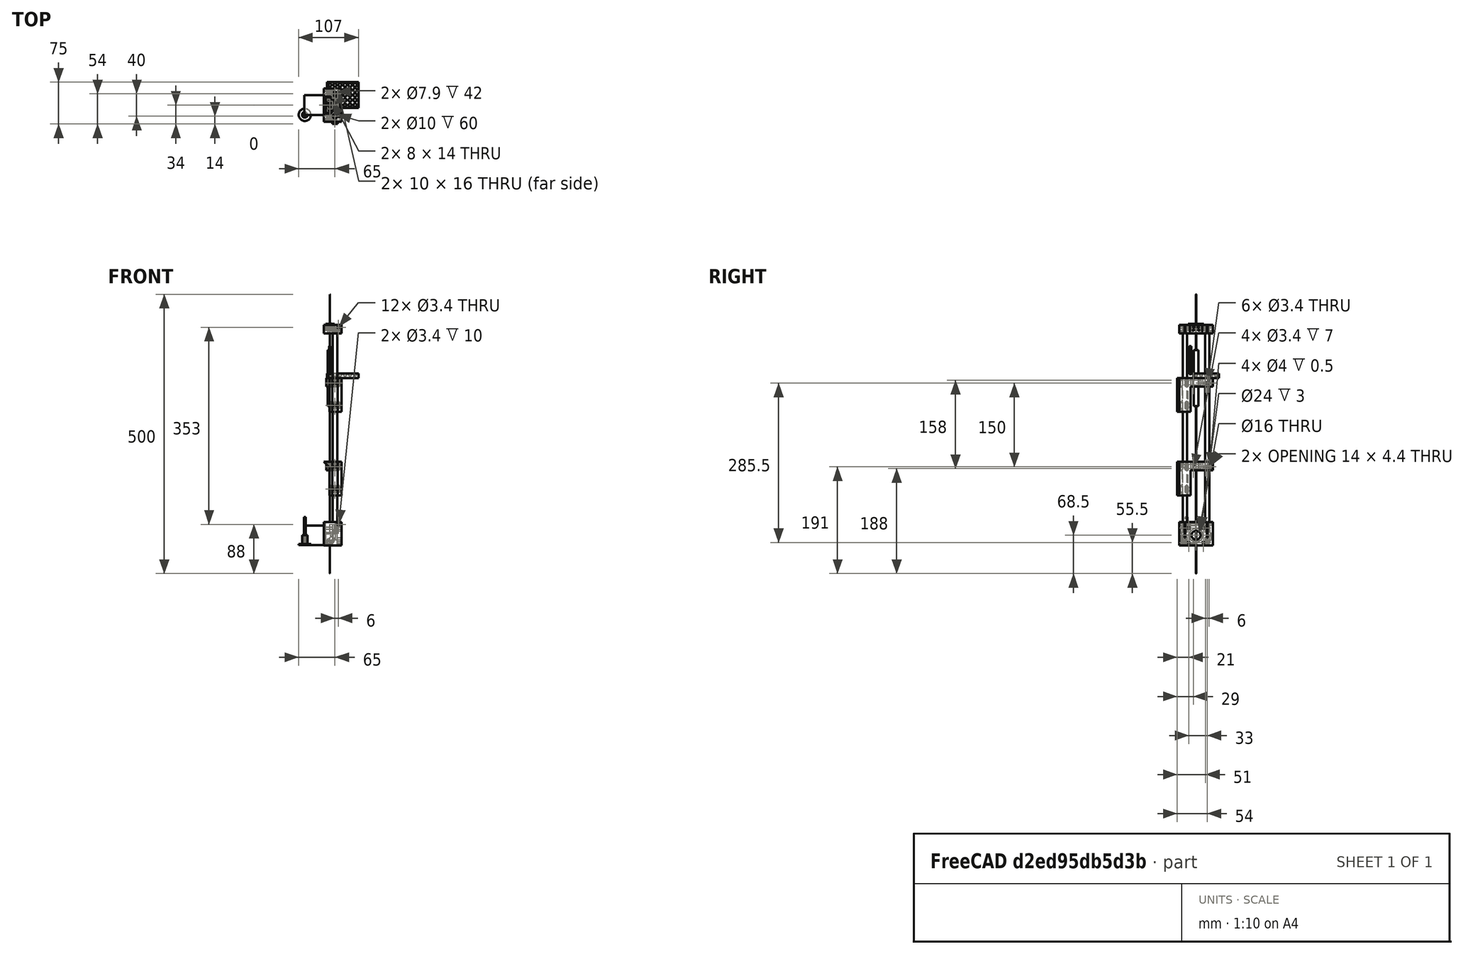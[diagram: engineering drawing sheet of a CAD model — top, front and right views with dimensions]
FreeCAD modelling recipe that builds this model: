
FCSTD DOCUMENT  (FreeCAD 0.16R6703 (Git))
Label: lorenz
License: All rights reserved
LicenseURL: http://en.wikipedia.org/wiki/All_rights_reserved
objects: Part::Cut×73, Part::Feature×49, Part::Cylinder×34, Part::Box×32, Part::Fuse×28, Part::Chamfer×13, Part::Sphere×7, Part::Sweep×6, App::DocumentObjectGroup×5, Part::Mirroring×5, Part::Circle×3, Part::Cone×2, Part::MultiCommon×1
note: 253 computed .brp shape members not serialized (recipe doc carries the construction recipe); baked Part::Feature solids carry a one-line shape summary decoded from their .brp

FEATURE [Part::Sphere] Sphere
  Angle1 = -90
  Angle2 = 90
  Angle3 = 360
  Placement = pos=(0,0,6) rot=(0,0,1;0rad)
  Radius = 3
FEATURE [Part::Box] Box112015002017004007003  label="Cube089"
  Height = 8
  Length = 56
  Placement = pos=(-5,-5,0) rot=(0,0,1;0rad)
  Width = 46
FEATURE [Part::Feature] Sphere001 .. Sphere005  x5 (patterned run collapsed; names and placements below)
  shape: bbox 6 x 6 x 6 mm, 1 faces (baked)
  placements: 5 in arithmetic series — first pos=(9,0,6.3) rot=(0,0,1;0rad), step (9,0,0.3), last pos=(45,0,7.5) rot=(0,0,1;0rad)
FEATURE [Part::Sphere] Sphere006
  Angle1 = -90
  Angle2 = 90
  Angle3 = 360
  Placement = pos=(0,9,6) rot=(0,0,1;0rad)
  Radius = 3.1
FEATURE [Part::Feature] Sphere006001 .. Sphere006005  x5 (patterned run collapsed; names and placements below)
  shape: bbox 6.2 x 6.2 x 6.2 mm, 1 faces (baked)
  placements: 5 in arithmetic series — first pos=(9,9,6.3) rot=(0,0,1;0rad), step (9,0,0.3), last pos=(45,9,7.5) rot=(0,0,1;0rad)
FEATURE [Part::Sphere] Sphere006006
  Angle1 = -90
  Angle2 = 90
  Angle3 = 360
  Placement = pos=(0,18,6) rot=(0,0,1;0rad)
  Radius = 3.2
FEATURE [Part::Feature] Sphere006006001 .. Sphere006006005  x5 (patterned run collapsed; names and placements below)
  shape: bbox 6.4 x 6.4 x 6.4 mm, 1 faces (baked)
  placements: 5 in arithmetic series — first pos=(9,18,6.3) rot=(0,0,1;0rad), step (9,0,0.3), last pos=(45,18,7.5) rot=(0,0,1;0rad)
FEATURE [Part::Sphere] Sphere006006006
  Angle1 = -90
  Angle2 = 90
  Angle3 = 360
  Placement = pos=(0,27,6) rot=(0,0,1;0rad)
  Radius = 3.3
FEATURE [Part::Feature] Sphere006006006001 .. Sphere006006006005  x5 (patterned run collapsed; names and placements below)
  shape: bbox 6.6 x 6.6 x 6.6 mm, 1 faces (baked)
  placements: 5 in arithmetic series — first pos=(9,27,6.3) rot=(0,0,1;0rad), step (9,0,0.3), last pos=(45,27,7.5) rot=(0,0,1;0rad)
FEATURE [Part::Sphere] Sphere006006006006
  Angle1 = -90
  Angle2 = 90
  Angle3 = 360
  Placement = pos=(0,36,6) rot=(0,0,1;0rad)
  Radius = 3.4
FEATURE [Part::Feature] Sphere006006006006001 .. Sphere006006006006005  x5 (patterned run collapsed; names and placements below)
  shape: bbox 6.8 x 6.8 x 6.8 mm, 1 faces (baked)
  placements: 5 in arithmetic series — first pos=(9,36,6.3) rot=(0,0,1;0rad), step (9,0,0.3), last pos=(45,36,7.5) rot=(0,0,1;0rad)
FEATURE [Part::Cut] Cut175
  Base = -> Box112015002017004007003
  Tool = -> Sphere
FEATURE [Part::Cut] Cut176
  Base = -> Cut175
  Tool = -> Sphere006006006006005
FEATURE [Part::Cut] Cut177
  Base = -> Cut176
  Tool = -> Sphere006006006006004
FEATURE [Part::Cut] Cut178
  Base = -> Cut177
  Tool = -> Sphere006006006006003
FEATURE [Part::Cut] Cut179
  Base = -> Cut178
  Tool = -> Sphere006006006006002
FEATURE [Part::Cut] Cut180
  Base = -> Cut179
  Tool = -> Sphere006006006006001
FEATURE [Part::Cut] Cut181
  Base = -> Cut180
  Tool = -> Sphere006006006006
FEATURE [Part::Cut] Cut182
  Base = -> Cut181
  Tool = -> Sphere006006006005
FEATURE [Part::Cut] Cut183
  Base = -> Cut182
  Tool = -> Sphere006006006004
FEATURE [Part::Cut] Cut184
  Base = -> Cut183
  Tool = -> Sphere006006006003
FEATURE [Part::Cut] Cut185
  Base = -> Cut184
  Tool = -> Sphere006006006002
FEATURE [Part::Cut] Cut186
  Base = -> Cut185
  Tool = -> Sphere006006006001
FEATURE [Part::Cut] Cut187
  Base = -> Cut186
  Tool = -> Sphere006006006
FEATURE [Part::Cut] Cut188
  Base = -> Cut187
  Tool = -> Sphere006006005
FEATURE [Part::Cut] Cut189
  Base = -> Cut188
  Tool = -> Sphere006006004
FEATURE [Part::Cut] Cut190
  Base = -> Cut189
  Tool = -> Sphere006006003
FEATURE [Part::Cut] Cut191
  Base = -> Cut190
  Tool = -> Sphere006006002
FEATURE [Part::Cut] Cut192
  Base = -> Cut191
  Tool = -> Sphere006006001
FEATURE [Part::Cut] Cut193
  Base = -> Cut192
  Tool = -> Sphere006006
FEATURE [Part::Cut] Cut194
  Base = -> Cut193
  Tool = -> Sphere006005
FEATURE [Part::Cut] Cut195
  Base = -> Cut194
  Tool = -> Sphere006004
FEATURE [Part::Cut] Cut196
  Base = -> Cut195
  Tool = -> Sphere006003
FEATURE [Part::Cut] Cut197
  Base = -> Cut196
  Tool = -> Sphere006002
FEATURE [Part::Cut] Cut198
  Base = -> Cut197
  Tool = -> Sphere006001
FEATURE [Part::Cut] Cut199
  Base = -> Cut198
  Tool = -> Sphere006
FEATURE [Part::Cut] Cut200
  Base = -> Cut199
  Tool = -> Sphere005
FEATURE [Part::Cut] Cut201
  Base = -> Cut200
  Tool = -> Sphere004
FEATURE [Part::Cut] Cut202
  Base = -> Cut201
  Tool = -> Sphere003
FEATURE [Part::Cut] Cut203
  Base = -> Cut202
  Tool = -> Sphere002
FEATURE [Part::Cut] Cut204
  Base = -> Cut203
  Tool = -> Sphere001
FEATURE [Part::Chamfer] Chamfer006012003  label="ball-socket-test"
  Base = -> Cut204
  Edges = 1 edges r=2: [Edge1]
FEATURE [App::DocumentObjectGroup] Group002  label="Experiments"
  Group = -> [Chamfer006012003]
FEATURE [Part::Box] Box112015002017004007004016  label="Cube099"
  Height = 14
  Length = 4.4
  Placement = pos=(-2.2,-2,-4) rot=(0,0,1;0rad)
  Width = 4
FEATURE [Part::Chamfer] Chamfer006012018
  Base = -> Box112015002017004007004016
  Edges = 1 edges r=2: [Edge6]
FEATURE [Part::Chamfer] Chamfer006012019
  Base = -> Chamfer006012018
  Edges = 1 edges r=2: [Edge15]
  Placement = pos=(0,0,2) rot=(0,0,1;0rad)
FEATURE [Part::Chamfer] Chamfer003
  Base = -> Chamfer006012019
  Edges = 1 edges r=2: [Edge14]
FEATURE [Part::Chamfer] Chamfer006012020  label="PTFE-slot-002"
  Base = -> Chamfer003
  Edges = 1 edges r=2: [Edge16]
  Placement = pos=(0,-6.25,0) rot=(0,0,1;0rad)
FEATURE [Part::Feature] Fusion051010010012015014001  label="reactor-slot-1"
  Placement = pos=(5.41266,3.125,0) rot=(0,0,1;2.0944rad)
  shape: bbox 5.997 x 5.887 x 14 mm, 14 faces (baked)
FEATURE [Part::Feature] Fusion051010010012015014002  label="reactor-slot-2"
  Placement = pos=(-5.41266,3.125,0) rot=(0,0,1;4.18879rad)
  shape: bbox 5.997 x 5.887 x 14 mm, 14 faces (baked)
FEATURE [Part::Cylinder] Cylinder054029  label="M4-adjuster"
  Angle = 360
  Height = 20
  Placement = pos=(0,-5,5) rot=(1,0,0;1.5708rad)
  Radius = 1.7
FEATURE [Part::Fuse] Fusion051010010012015014003  label="adjuster-slot"
  Base = -> Chamfer006012020
  Tool = -> Cylinder054029
FEATURE [Part::Cylinder] Cylinder054031  label="steel002"
  Angle = 360
  Height = 200
  Placement = pos=(0,0,-100) rot=(0,0,1;0rad)
  Radius = 5
FEATURE [Part::Box] Box112015002017004007004017  label="Cube100"
  Height = 16
  Length = 16
  Placement = pos=(0,-30,0) rot=(0,0,1;0rad)
  Width = 60
FEATURE [Part::Box] Box112015002017004007004018  label="Cube101"
  Height = 20
  Length = 100
  Placement = pos=(-50,-50,-28) rot=(0,0,1;0rad)
  Width = 100
FEATURE [Part::Sphere] Sphere006006006006008
  Angle1 = -90
  Angle2 = 90
  Angle3 = 360
  Placement = pos=(8,25,1.2) rot=(0,0,1;0rad)
  Radius = 3.05
FEATURE [Part::Sphere] Sphere006006006006009
  Angle1 = -90
  Angle2 = 90
  Angle3 = 360
  Placement = pos=(8,-25,1.2) rot=(0,0,1;0rad)
  Radius = 3.05
FEATURE [Part::Cut] Cut253
  Base = -> Box112015002017004007004017
  Tool = -> Sphere006006006006008
FEATURE [Part::Cut] Cut254
  Base = -> Cut253
  Placement = pos=(-22,0,3) rot=(0,1,0;2.35619rad)
  Tool = -> Sphere006006006006009
FEATURE [Part::Cut] Cut255  label="socket-bar001"
  Base = -> Cut254
  Placement = pos=(22,0,-8) rot=(1,0,0;3.14159rad)
  Tool = -> Box112015002017004007004018
FEATURE [Part::Fuse] Fusion051010010012015014004
  Base = -> Fusion051010010012015014001
  Tool = -> Fusion051010010012015014002
FEATURE [Part::Fuse] Fusion051010010012015014005
  Base = -> Fusion051010010012015014003
  Tool = -> Fusion051010010012015014004
FEATURE [Part::Fuse] Fusion051010010012015014006  label="bearing-cavity-3a"
  Base = -> Cylinder054031
  Placement = pos=(9,-20,-4) rot=(0,1,0;3.14159rad)
  Tool = -> Fusion051010010012015014005
FEATURE [Part::Box] Box112015002017004007004019  label="Cube102"
  Height = 14
  Length = 4.4
  Placement = pos=(-2.2,-2,-4) rot=(0,0,1;0rad)
  Width = 4
FEATURE [Part::Chamfer] Chamfer006012021
  Base = -> Box112015002017004007004019
  Edges = 1 edges r=2: [Edge6]
FEATURE [Part::Chamfer] Chamfer006012022
  Base = -> Chamfer006012021
  Edges = 1 edges r=2: [Edge15]
  Placement = pos=(0,0,2) rot=(0,0,1;0rad)
FEATURE [Part::Chamfer] Chamfer006012023
  Base = -> Chamfer006012022
  Edges = 1 edges r=2: [Edge14]
FEATURE [Part::Chamfer] Chamfer006012024  label="PTFE-slot-003"
  Base = -> Chamfer006012023
  Edges = 1 edges r=2: [Edge16]
  Placement = pos=(0,-6.25,0) rot=(0,0,1;0rad)
FEATURE [Part::Cylinder] Cylinder054032  label="M4-adjuster001"
  Angle = 360
  Height = 20
  Placement = pos=(0,-5,5) rot=(1,0,0;1.5708rad)
  Radius = 1.7
FEATURE [Part::Fuse] Fusion051010010012015014007  label="adjuster-slot001"
  Base = -> Chamfer006012024
  Placement = pos=(-5,0,0) rot=(0,1,0;1.5708rad)
  Tool = -> Cylinder054032
FEATURE [Part::Feature] Fusion051010010012015014008  label="reactor-slot-003"
  Placement = pos=(-5,6.25,-6.13174e-07) rot=(0.707107,0,0.707107;3.14159rad)
  shape: bbox 14 x 4.5 x 4.4 mm, 14 faces (baked)
FEATURE [Part::Box] Box112015002017004007004020  label="Cube103"
  Height = 200
  Length = 16
  Placement = pos=(-8,-5,-100) rot=(0,0,1;0rad)
  Width = 10
FEATURE [Part::Fuse] Fusion051010010012015014009
  Base = -> Fusion051010010012015014008
  Tool = -> Box112015002017004007004020
FEATURE [Part::Fuse] Fusion051010010012015014010  label="bearing-cavity-2a"
  Base = -> Fusion051010010012015014007
  Placement = pos=(9,20,-9) rot=(-0.707107,0.707107,0;3.14159rad)
  Tool = -> Fusion051010010012015014009
FEATURE [Part::Fuse] Fusion051010010012015014013  label="bearing-cavity-3a001"
  Base = -> Cylinder054031
  Placement = pos=(9,-20,-44) rot=(0,1,0;3.14159rad)
  Tool = -> Fusion051010010012015014005
FEATURE [Part::Box] Box112015002017004007004021  label="Cube104"
  Height = 60
  Length = 22
  Placement = pos=(-1,-30,0) rot=(0,0,1;0rad)
  Width = 60
FEATURE [Part::Box] Box112015002017004007004022  label="Cube105"
  Height = 60
  Length = 24
  Placement = pos=(-2,-50,15) rot=(0,0,1;0rad)
  Width = 60
FEATURE [Part::Box] Box112015002017004007004023  label="Cube106"
  Height = 60
  Length = 10
  Placement = pos=(4,24,0) rot=(0,0,1;0rad)
  Width = 10
FEATURE [Part::Fuse] Fusion051010010012015014014
  Base = -> Box112015002017004007004021
  Tool = -> Box112015002017004007004023
FEATURE [Part::Cut] Cut256
  Base = -> Fusion051010010012015014014
  Placement = pos=(0,0,0) rot=(1,0,0;3.14159rad)
  Tool = -> Box112015002017004007004022
FEATURE [Part::Cylinder] Cylinder054033  label="centreline"
  Angle = 360
  Height = 500
  Placement = pos=(0,0,-350) rot=(0,0,1;0rad)
  Radius = 0.1
FEATURE [Part::Box] Box112015002017004007004024  label="wire-clamp-slot001"
  Height = 30
  Length = 1
  Placement = pos=(-0.5,-6,-19) rot=(0,0,1;0rad)
  Width = 2
FEATURE [Part::Cylinder] Cylinder054035  label="wire-clamp-screw-hole-1"
  Angle = 360
  Height = 10
  Placement = pos=(-9.5,-5,-4) rot=(0,1,0;1.5708rad)
  Radius = 1.7
FEATURE [Part::Cylinder] Cylinder054036  label="wire-clamp-screw-hole-2"
  Angle = 360
  Height = 10
  Placement = pos=(-9.5,-5,-12) rot=(0,1,0;1.5708rad)
  Radius = 1.7
FEATURE [Part::Box] Box112015002017004007004025  label="Cube108"
  Height = 15
  Length = 6
  Placement = pos=(-6.5,-9,-15) rot=(0,0,1;0rad)
  Width = 18
FEATURE [Part::Box] Box112015002017004007004026  label="wire-slot"
  Height = 30
  Length = 8
  Placement = pos=(-4,4,-19) rot=(0,0,1;0rad)
  Width = 2
FEATURE [Part::Cylinder] Cylinder054037  label="steel-3"
  Angle = 360
  Height = 395
  Placement = pos=(9,-20,-300) rot=(0,0,1;0rad)
  Radius = 4
FEATURE [Part::Cylinder] Cylinder054038  label="steel-2"
  Angle = 360
  Height = 395
  Placement = pos=(9,20,-300) rot=(0,0,1;0rad)
  Radius = 4
FEATURE [Part::Box] Box112015002017004007004027  label="Cube110"
  Height = 42
  Length = 32
  Placement = pos=(-11,-30,-1) rot=(0,0,1;0rad)
  Width = 60
FEATURE [Part::Box] Box112015002017004007004028  label="Cube111"
  Height = 35
  Length = 35
  Placement = pos=(-46,-17.5,-299) rot=(0,0,1;0rad)
  Width = 35
FEATURE [Part::Cylinder] Cylinder054039  label="drive"
  Angle = 360
  Height = 18
  Placement = pos=(-45,-17.5,-299) rot=(0,0,1;0rad)
  Radius = 5
FEATURE [Part::Cylinder] Cylinder054040  label="boss"
  Angle = 360
  Height = 2
  Placement = pos=(-45,-17.5,-299) rot=(0,0,1;0rad)
  Radius = 11
FEATURE [Part::Cylinder] Cylinder054041  label="M3-1"
  Angle = 360
  Height = 50
  Placement = pos=(-45,-17.5,-299) rot=(0,0,1;0rad)
  Radius = 1.7
FEATURE [Part::Cylinder] Cylinder054042  label="M3-2"
  Angle = 360
  Height = 50
  Placement = pos=(-45,-17.5,-299) rot=(0,0,1;0rad)
  Radius = 1.7
FEATURE [Part::Cylinder] Cylinder054043  label="M3-3"
  Angle = 360
  Height = 50
  Placement = pos=(-45,-17.5,-299) rot=(0,0,1;0rad)
  Radius = 1.7
FEATURE [Part::Cylinder] Cylinder054044  label="M3-4"
  Angle = 360
  Height = 50
  Placement = pos=(-45,-17.5,-299) rot=(0,0,1;0rad)
  Radius = 1.7
FEATURE [App::DocumentObjectGroup] Group005  label="NEMA-14"
  Group = -> [Box112015002017004007004028,Cylinder054039,Cylinder054040,Cylinder054041,Cylinder054042,Cylinder054043,Cylinder054044]
FEATURE [Part::Cylinder] Cylinder054045  label="boss001"
  Angle = 360
  Height = 3
  Placement = pos=(-11,0,17.5) rot=(0,1,0;1.5708rad)
  Radius = 12
FEATURE [Part::Cut] Cut264
  Base = -> Box112015002017004007004027
  Tool = -> Cylinder054045
FEATURE [Part::Cylinder] Cylinder054046  label="M3-005"
  Angle = 360
  Height = 50
  Placement = pos=(-12,13,30.5) rot=(0,1,0;1.5708rad)
  Radius = 1.7
FEATURE [Part::Cylinder] Cylinder054047  label="M3-006"
  Angle = 360
  Height = 50
  Placement = pos=(-12,-13,4.5) rot=(0,1,0;1.5708rad)
  Radius = 1.7
FEATURE [Part::Cylinder] Cylinder054048  label="M3-007"
  Angle = 360
  Height = 50
  Placement = pos=(-12,13,4.5) rot=(0,1,0;1.5708rad)
  Radius = 1.7
FEATURE [Part::Cylinder] Cylinder054049  label="M3-008"
  Angle = 360
  Height = 50
  Placement = pos=(-12,-13,30.5) rot=(0,1,0;1.5708rad)
  Radius = 1.7
FEATURE [Part::Cut] Cut265
  Base = -> Cut264
  Tool = -> Cylinder054046
FEATURE [Part::Cut] Cut266
  Base = -> Cut265
  Tool = -> Cylinder054049
FEATURE [Part::Cut] Cut267
  Base = -> Cut266
  Tool = -> Cylinder054048
FEATURE [Part::Cut] Cut268
  Base = -> Cut267
  Tool = -> Cylinder054047
FEATURE [Part::Cylinder] Cylinder054050  label="drive001"
  Angle = 360
  Height = 40
  Placement = pos=(-9,0,17.5) rot=(0,1,0;1.5708rad)
  Radius = 8
FEATURE [Part::Cut] Cut269
  Base = -> Cut268
  Tool = -> Cylinder054050
FEATURE [Part::Box] Box112015002017004007004029  label="Cube112"
  Height = 50
  Length = 18
  Placement = pos=(-8,-10,9) rot=(0,0,1;0rad)
  Width = 20
FEATURE [Part::Cut] Cut270
  Base = -> Cut269
  Tool = -> Box112015002017004007004029
FEATURE [Part::Cylinder] Cylinder054051  label="grub-003"
  Angle = 360
  Height = 30
  Placement = pos=(-28,26,32) rot=(1,0,0;1.5708rad)
  Radius = 1.7
FEATURE [Part::Box] Box112015002017004007004030  label="Cube113"
  Height = 33
  Length = 5.3
  Placement = pos=(-30.65,6,29) rot=(0,0,1;0rad)
  Width = 2.5
FEATURE [Part::Fuse] Fusion051010010012015014017  label="nut-trap"
  Base = -> Cylinder054051
  Placement = pos=(43,5,5) rot=(0,0,1;0rad)
  Tool = -> Box112015002017004007004030
FEATURE [Part::Box] Box112015002017004007004031  label="Cube114"
  Height = 50
  Length = 15
  Placement = pos=(10,19.25,13) rot=(0,0,1;0rad)
  Width = 1.5
FEATURE [Part::Fuse] Fusion051010010012015014018  label="rod-clamp"
  Base = -> Fusion051010010012015014017
  Tool = -> Box112015002017004007004031
FEATURE [Part::Cylinder] Cylinder054052  label="steel-004"
  Angle = 360
  Height = 395
  Placement = pos=(9,20,-300) rot=(0,0,1;0rad)
  Radius = 3.95
FEATURE [Part::Fuse] Fusion051010010012015014019  label="rod-and-clamp"
  Base = -> Fusion051010010012015014018
  Tool = -> Cylinder054052
FEATURE [Part::Fuse] Fusion051010010012015014020  label="rod-and-clamp001"
  Base = -> Fusion051010010012015014018
  Tool = -> Cylinder054052
FEATURE [Part::Mirroring] Part__Mirroring005006  label="rod-and-clamp (Mirror #7)"
  Base = (0,0,0)
  Normal = (0,1,0)
  Source = -> Fusion051010010012015014019
FEATURE [Part::Cut] Cut271
  Base = -> Cut270
  Tool = -> Fusion051010010012015014020
FEATURE [Part::Cut] Cut272  label="base-block-b"
  Base = -> Cut271
  Placement = pos=(0,0,-299) rot=(0,0,1;0rad)
  Tool = -> Part__Mirroring005006
FEATURE [Part::Box] Box112015002017004007004032  label="Cube115"
  Height = 15
  Length = 32
  Placement = pos=(-11,-30,26) rot=(0,0,1;0rad)
  Width = 60
FEATURE [Part::Cylinder] Cylinder054053  label="grub-004"
  Angle = 360
  Height = 30
  Placement = pos=(-28,31,32) rot=(1,0,0;1.5708rad)
  Radius = 1.7
FEATURE [Part::Box] Box112015002017004007004034  label="Cube117"
  Height = 33
  Length = 5.3
  Placement = pos=(-30.65,6,29) rot=(0,0,1;0rad)
  Width = 2.5
FEATURE [Part::Fuse] Fusion051010010012015014021  label="nut-trap001"
  Base = -> Cylinder054053
  Placement = pos=(43,7,5) rot=(0,0,1;0rad)
  Tool = -> Box112015002017004007004034
FEATURE [Part::Box] Box112015002017004007004035  label="Cube118"
  Height = 50
  Length = 15
  Placement = pos=(10,19.25,-4) rot=(0,0,1;0rad)
  Width = 1.5
FEATURE [Part::Fuse] Fusion051010010012015014022  label="rod-clamp001"
  Base = -> Fusion051010010012015014021
  Tool = -> Box112015002017004007004035
FEATURE [Part::Cylinder] Cylinder054054  label="steel-005"
  Angle = 360
  Height = 395
  Placement = pos=(9,20,-300) rot=(0,0,1;0rad)
  Radius = 3.9
FEATURE [Part::Fuse] Fusion051010010012015014023  label="rod-and-clamp002"
  Base = -> Fusion051010010012015014022
  Tool = -> Cylinder054054
FEATURE [Part::Fuse] Fusion051010010012015014024  label="rod-and-clamp003"
  Base = -> Fusion051010010012015014022
  Tool = -> Cylinder054054
FEATURE [Part::Mirroring] Part__Mirroring005007  label="rod-and-clamp (Mirror #7)001"
  Base = (0,0,0)
  Normal = (0,1,0)
  Source = -> Fusion051010010012015014023
FEATURE [Part::Cylinder] Cylinder054055  label="V-bearing"
  Angle = 360
  Height = 4
  Placement = pos=(-2,0,92) rot=(0,1,0;1.5708rad)
  Radius = 6
FEATURE [Part::Cone] Cone011
  Angle = 360
  Height = 3
  Placement = pos=(0,0,2) rot=(0,0,1;0rad)
  Radius1 = 2.5
  Radius2 = 5.5
FEATURE [Part::Mirroring] Part__Mirroring005008  label="Cone011 (Mirror #9)"
  Base = (0,0,0)
  Normal = (0,0,1)
  Placement = pos=(0.1,0,38) rot=(0,1,0;1.5708rad)
  Source = -> Cone011
FEATURE [Part::Cone] Cone012
  Angle = 360
  Height = 3
  Placement = pos=(1.9,0,38) rot=(0,1,0;1.5708rad)
  Radius1 = 2.5
  Radius2 = 5.5
FEATURE [Part::Box] Box112015002017004007004036  label="Cube119"
  Height = 8
  Length = 60
  Placement = pos=(-4,-7,68) rot=(0,1,0;1.5708rad)
  Width = 14
FEATURE [Part::Box] Box112015002017004007004037  label="Cube120"
  Height = 16
  Length = 10
  Placement = pos=(-8,-14,43) rot=(0,1,0;1.5708rad)
  Width = 28
FEATURE [Part::Cylinder] Cylinder054056  label="bearing-M3"
  Angle = 360
  Height = 40
  Placement = pos=(-20,0,38) rot=(0,1,0;1.5708rad)
  Radius = 1.4
FEATURE [Part::Cylinder] Cylinder054057  label="Cylinder054065"
  Angle = 360
  Height = 10
  Radius = 5
FEATURE [Part::Box] Box112015002017004007004038  label="Cube121"
  Height = 12
  Length = 10
  Placement = pos=(-5,2.75,-1) rot=(0,0,1;0rad)
  Width = 10
FEATURE [Part::Feature] Box112015002017004007004038001
  Placement = pos=(-4.88157,-2.95513,-1) rot=(0,0,1;1.0472rad)
  shape: bbox 13.66 x 13.66 x 12 mm, 6 faces (baked)
FEATURE [Part::Feature] Box112015002017004007004038002
  Placement = pos=(0.11843,-5.70513,-1) rot=(0,0,1;2.0944rad)
  shape: bbox 13.66 x 13.66 x 12 mm, 6 faces (baked)
FEATURE [Part::Feature] Box112015002017004007004038003
  Placement = pos=(5,-2.75,-1) rot=(0,0,1;3.14159rad)
  shape: bbox 10 x 10 x 12 mm, 6 faces (baked)
FEATURE [Part::Feature] Box112015002017004007004038004
  Placement = pos=(4.88157,2.95513,-1) rot=(0,0,1;4.18879rad)
  shape: bbox 13.66 x 13.66 x 12 mm, 6 faces (baked)
FEATURE [Part::Feature] Box112015002017004007004038005
  Placement = pos=(-0.11843,5.70513,-1) rot=(0,0,-1;1.0472rad)
  shape: bbox 13.66 x 13.66 x 12 mm, 6 faces (baked)
FEATURE [Part::Cut] Cut273
  Base = -> Cylinder054057
  Tool = -> Box112015002017004007004038
FEATURE [Part::Cut] Cut274
  Base = -> Cut273
  Tool = -> Box112015002017004007004038005
FEATURE [Part::Cut] Cut275
  Base = -> Cut274
  Tool = -> Box112015002017004007004038004
FEATURE [Part::Cut] Cut276
  Base = -> Cut275
  Tool = -> Box112015002017004007004038003
FEATURE [Part::Cut] Cut277
  Base = -> Cut276
  Tool = -> Box112015002017004007004038002
FEATURE [Part::Cut] Cut278
  Base = -> Cut277
  Tool = -> Box112015002017004007004038001
FEATURE [Part::Cylinder] Cylinder054058  label="Cylinder054066"
  Angle = 360
  Height = 50
  Placement = pos=(0,0,-20) rot=(0,0,1;0rad)
  Radius = 1.7
FEATURE [Part::Fuse] Fusion051010010012015014025  label="M3-nut-hole"
  Base = -> Cut278
  Placement = pos=(0,-10.5,27) rot=(0,0,1;0rad)
  Tool = -> Cylinder054058
FEATURE [App::DocumentObjectGroup] Group004  label="Temporary"
  Group = -> [Fusion051010010012015014025]
FEATURE [Part::Box] Box112015002017004007004038006  label="Cube122"
  Height = 18
  Length = 10
  Placement = pos=(-9,-15,42) rot=(0,1,0;1.5708rad)
  Width = 30
FEATURE [Part::Box] Box112015002017004007004038007  label="Cube123"
  Height = 8
  Length = 60
  Placement = pos=(-4,-7,68) rot=(0,1,0;1.5708rad)
  Width = 14
FEATURE [Part::Cylinder] Cylinder054059  label="Cylinder054067"
  Angle = 360
  Height = 20
  Placement = pos=(-10,11,32) rot=(0,1,0;1.5708rad)
  Radius = 2
FEATURE [Part::Fuse] Fusion051010010012015014027  label="bearing-cones"
  Base = -> Part__Mirroring005008
  Tool = -> Cone012
FEATURE [Part::Box] Box112015002017004007004038008  label="Cube124"
  Height = 16
  Length = 10
  Placement = pos=(-8,-14,43) rot=(0,1,0;1.5708rad)
  Width = 28
FEATURE [Part::MultiCommon] Common010  label="bearing-cones-truncated"
  Shapes = -> [Box112015002017004007004038008,Fusion051010010012015014027]
FEATURE [Part::Fuse] Fusion051010010012015014029
  Base = -> Cut256
  Tool = -> Box112015002017004007004025
FEATURE [Part::Cut] Cut286
  Base = -> Fusion051010010012015014029
  Tool = -> Fusion051010010012015014013
FEATURE [Part::Cut] Cut287
  Base = -> Cut286
  Tool = -> Fusion051010010012015014006
FEATURE [Part::Cut] Cut288
  Base = -> Cut287
  Tool = -> Fusion051010010012015014010
FEATURE [Part::Cut] Cut289
  Base = -> Cut288
  Tool = -> Cylinder054036
FEATURE [Part::Cut] Cut290
  Base = -> Cut289
  Tool = -> Cylinder054035
FEATURE [Part::Cut] Cut291
  Base = -> Cut290
  Tool = -> Box112015002017004007004024
FEATURE [Part::Cut] Cut292  label="slider-blank"
  Base = -> Cut291
  Tool = -> Box112015002017004007004026
FEATURE [Part::Cut] Cut293  label="slider-blank001"
  Base = -> Cut291
  Tool = -> Box112015002017004007004026
FEATURE [Part::Box] Box112015002017004007004038009  label="Cube125"
  Height = 15
  Length = 31
  Placement = pos=(-15.5,-17,-13) rot=(0,0,1;0rad)
  Width = 34
FEATURE [Part::Box] Box112015002017004007004038010  label="Cube126"
  Height = 15
  Length = 31
  Placement = pos=(0.5,-35,-13) rot=(0,0,1;0rad)
  Width = 70
FEATURE [Part::Fuse] Fusion051010010012015014030
  Base = -> Box112015002017004007004038009
  Tool = -> Box112015002017004007004038010
FEATURE [Part::Cut] Cut294  label="ball-socket-tabs"
  Base = -> Cut255
  Tool = -> Fusion051010010012015014030
FEATURE [Part::Fuse] Fusion051010010012015014031  label="delta-slider"
  Base = -> Cut293
  Placement = pos=(0,0,-150) rot=(0,0,1;0rad)
  Tool = -> Cut294
FEATURE [Part::Cylinder] Cylinder054060  label="Cylinder054091"
  Angle = 360
  Height = 20
  Placement = pos=(-10,11,32) rot=(0,1,0;1.5708rad)
  Radius = 2.2
FEATURE [Part::Cylinder] Cylinder054061  label="Cylinder054092"
  Angle = 360
  Height = 50
  Placement = pos=(0,-10.5,7) rot=(0,0,1;0rad)
  Radius = 1.3
FEATURE [Part::Box] Box112015002017004007004038011  label="Cube127"
  Height = 20
  Length = 10
  Placement = pos=(18,-11,78) rot=(0,0,1;0rad)
  Width = 22
FEATURE [Part::Cylinder] Cylinder054062  label="Cylinder054093"
  Angle = 360
  Height = 30
  Placement = pos=(11,4.75,86) rot=(0,1,0;1.5708rad)
  Radius = 1.1
FEATURE [Part::Cylinder] Cylinder054063  label="Cylinder054094"
  Angle = 360
  Height = 30
  Placement = pos=(11,-4.75,86) rot=(0,1,0;1.5708rad)
  Radius = 1.1
FEATURE [Part::Fuse] Fusion051010010012015014032
  Base = -> Box112015002017004007004038011
  Tool = -> Cylinder054062
FEATURE [Part::Fuse] Fusion051010010012015014033  label="microswitch-cavity"
  Base = -> Cylinder054063
  Tool = -> Fusion051010010012015014032
FEATURE [Part::Chamfer] Chamfer006012025
  Base = -> Box112015002017004007004037
  Edges = 1 edges r=8: [Edge12]
FEATURE [Part::Chamfer] Chamfer006012026
  Base = -> Chamfer006012025
  Edges = 1 edges r=8: [Edge7]
FEATURE [Part::Cut] Cut298
  Base = -> Chamfer006012026
  Tool = -> Box112015002017004007004036
FEATURE [Part::Fuse] Fusion051010010012015014034
  Base = -> Common010
  Tool = -> Cut298
FEATURE [Part::Cut] Cut299
  Base = -> Fusion051010010012015014034
  Tool = -> Cylinder054056
FEATURE [Part::Cut] Cut300
  Base = -> Cut299
  Tool = -> Cylinder054060
FEATURE [Part::Cut] Cut301  label="wire-tensioner"
  Base = -> Cut300
  Placement = pos=(0,0,54) rot=(0,0,1;0rad)
  Tool = -> Cylinder054061
FEATURE [Part::Chamfer] Chamfer006012027
  Base = -> Box112015002017004007004038006
  Edges = 1 edges r=8: [Edge10]
FEATURE [Part::Chamfer] Chamfer006012028
  Base = -> Chamfer006012027
  Edges = 1 edges r=8: [Edge13]
FEATURE [Part::Cut] Cut302
  Base = -> Box112015002017004007004032
  Tool = -> Chamfer006012028
FEATURE [Part::Cut] Cut303
  Base = -> Cut302
  Tool = -> Box112015002017004007004038007
FEATURE [Part::Fuse] Fusion051010010012015014035
  Base = -> Cylinder054059
  Tool = -> Cut303
FEATURE [Part::Cut] Cut304
  Base = -> Fusion051010010012015014035
  Tool = -> Part__Mirroring005007
FEATURE [Part::Cut] Cut305
  Base = -> Cut304
  Placement = pos=(0,0,54) rot=(0,0,1;0rad)
  Tool = -> Fusion051010010012015014024
FEATURE [Part::Cut] Cut306  label="top-block-a"
  Base = -> Cut305
  Tool = -> Fusion051010010012015014033
FEATURE [Part::Box] Box112015002017004007004038026  label="crimp-hole-1"
  Height = 2
  Length = 29
  Placement = pos=(-28,-27,-278.5) rot=(0,0,1;0rad)
  Width = 2
FEATURE [Part::Box] Box112015002017004007004038027  label="crimp-hole-2"
  Height = 2
  Length = 29
  Placement = pos=(-28,-27,-283.58) rot=(0,0,1;0rad)
  Width = 2
FEATURE [Part::Cylinder] Cylinder054028  label="steel"
  Angle = 360
  Height = 100
  Placement = pos=(0,0,-50) rot=(0,0,1;0rad)
  Radius = 4
FEATURE [Part::Circle] Circle
  Angle0 = 0
  Angle1 = 360
  Placement = pos=(1,-26,-297.5) rot=(0,1,0;1.5708rad)
  Radius = 0.7
FEATURE [Part::Box] Box112015002017004007004038040  label="tiny-point-cube"
  Height = 0.2
  Length = 0.2
  Placement = pos=(11,-20,84) rot=(0,0,1;0rad)
  Width = 0.2
FEATURE [Part::Feature] Shape
  shape: bbox 8.954 x 5.598 x 34.27 mm, 0 faces, 0 solids (baked)
FEATURE [Part::Feature] Shape001
  shape: bbox 11.02 x 51.23 x 37.09 mm, 0 faces, 0 solids (baked)
FEATURE [Part::Circle] Circle001
  Angle0 = 0
  Angle1 = 360
  Placement = pos=(1,-26,-297.5) rot=(0,1,0;1.5708rad)
  Radius = 1.2
FEATURE [Part::Feature] Face
  Placement = pos=(0,0,20) rot=(0,0,1;0rad)
  shape: bbox 2e-07 x 2.603 x 2.778 mm, 1 faces, 0 solids (baked)
FEATURE [Part::Feature] Shape002
  shape: bbox 24.53 x 3.067 x 36 mm, 0 faces, 0 solids (baked)
FEATURE [Part::Circle] Circle002
  Angle0 = 0
  Angle1 = 360
  Placement = pos=(-15,23,-294) rot=(0,1,0;1.5708rad)
  Radius = 2.5
FEATURE [Part::Feature] Face002
  shape: bbox 2e-07 x 7.388 x 7.38 mm, 1 faces, 0 solids (baked)
FEATURE [Part::Sweep] Sweep002
  Frenet = false
  Sections = -> [Face002]
  Solid = true
  Spine = -> Shape002 [Edge1]
  Transition = 1
FEATURE [Part::Mirroring] Part__Mirroring  label="Sweep002 (Mirror #5)"
  Base = (0,0,0)
  Normal = (0,1,0)
  Source = -> Sweep002
FEATURE [Part::Sweep] Sweep003
  Frenet = false
  Sections = -> [Face002]
  Solid = true
  Spine = -> Shape002 [Edge1]
  Transition = 1
FEATURE [Part::Cut] Cut338
  Base = -> Cut272
  Tool = -> Sweep003
FEATURE [Part::Cut] Cut339
  Base = -> Cut338
  Tool = -> Part__Mirroring
FEATURE [Part::Feature] Shape003
  shape: bbox 8.807 x 6.01 x 17.13 mm, 0 faces, 0 solids (baked)
FEATURE [Part::Sweep] Sweep
  Frenet = false
  Sections = -> [Face]
  Solid = true
  Spine = -> Shape003 [Edge1]
  Transition = 1
FEATURE [Part::Fuse] Fusion  label="wire-hole-1"
  Base = -> Box112015002017004007004038026
  Tool = -> Sweep
FEATURE [Part::Feature] Shape004
  shape: bbox 8.864 x 52.92 x 37.82 mm, 0 faces, 0 solids (baked)
FEATURE [Part::Feature] Shape005
  shape: bbox 9.107 x 52.63 x 38.07 mm, 0 faces, 0 solids (baked)
FEATURE [Part::Feature] Face003
  Placement = pos=(0,0,14.92) rot=(0,0,1;0rad)
  shape: bbox 2e-07 x 2.603 x 2.778 mm, 1 faces, 0 solids (baked)
FEATURE [Part::Sweep] Sweep005
  Frenet = false
  Sections = -> [Face003]
  Solid = true
  Spine = -> Shape005 [Edge1]
  Transition = 1
FEATURE [Part::Fuse] Fusion051010010012015014039  label="wire-hole-2"
  Base = -> Box112015002017004007004038027
  Tool = -> Sweep005
FEATURE [Part::Cut] Cut
  Base = -> Cut339
  Tool = -> Fusion
FEATURE [Part::Cut] Cut340  label="bottom-block"
  Base = -> Cut
  Tool = -> Fusion051010010012015014039
FEATURE [Part::Feature] Face001
  Placement = pos=(18,22,389) rot=(0,0,1;0rad)
  shape: bbox 2e-07 x 2.603 x 2.778 mm, 1 faces, 0 solids (baked)
FEATURE [Part::Feature] Shape006
  shape: bbox 18.54 x 23.52 x 8.185 mm, 0 faces, 0 solids (baked)
FEATURE [Part::Feature] Face004
  Placement = pos=(17,22,389) rot=(0,0,1;0rad)
  shape: bbox 2e-07 x 2.603 x 2.778 mm, 1 faces, 0 solids (baked)
FEATURE [Part::Feature] Shape007
  shape: bbox 18.54 x 23.52 x 8.185 mm, 0 faces, 0 solids (baked)
FEATURE [Part::Feature] Shape008
  shape: bbox 19.54 x 23.73 x 8.185 mm, 0 faces, 0 solids (baked)
FEATURE [Part::Sweep] Sweep006  label="top-wire-1"
  Frenet = false
  Sections = -> [Face001]
  Solid = true
  Spine = -> Shape008 [Edge1]
  Transition = 1
FEATURE [Part::Feature] Face005
  Placement = pos=(18,22,389) rot=(0,0,1;0rad)
  shape: bbox 2e-07 x 2.603 x 2.778 mm, 1 faces, 0 solids (baked)
FEATURE [Part::Feature] Shape009
  shape: bbox 19.54 x 23.73 x 8.185 mm, 0 faces, 0 solids (baked)
FEATURE [App::DocumentObjectGroup] Group  label="Construction"
  Group = -> [Cylinder054033,Cylinder054028,Cut292,Box112015002017004007004038040,Shape,Circle,Shape001,Circle001,Circle002,Shape002,Shape003,Shape004,Shape005,Shape006,Shape007,Face004,Shape008,Shape009]
FEATURE [Part::Sweep] Sweep007
  Frenet = false
  Sections = -> [Face005]
  Solid = true
  Spine = -> Shape009 [Edge1]
  Transition = 1
FEATURE [Part::Mirroring] Part__Mirroring005009  label="top-wire-2"
  Base = (0,0,0)
  Normal = (0,1,0)
  Source = -> Sweep007
FEATURE [Part::Cut] Cut341
  Base = -> Cut306
  Tool = -> Sweep006
FEATURE [Part::Cut] Cut342  label="top-block"
  Base = -> Cut341
  Tool = -> Part__Mirroring005009
FEATURE [App::DocumentObjectGroup] Group006  label="current"
  Group = -> [Cylinder054037,Cylinder054038,Cylinder054055,Fusion051010010012015014031,Cut301,Cut340,Cut342]
